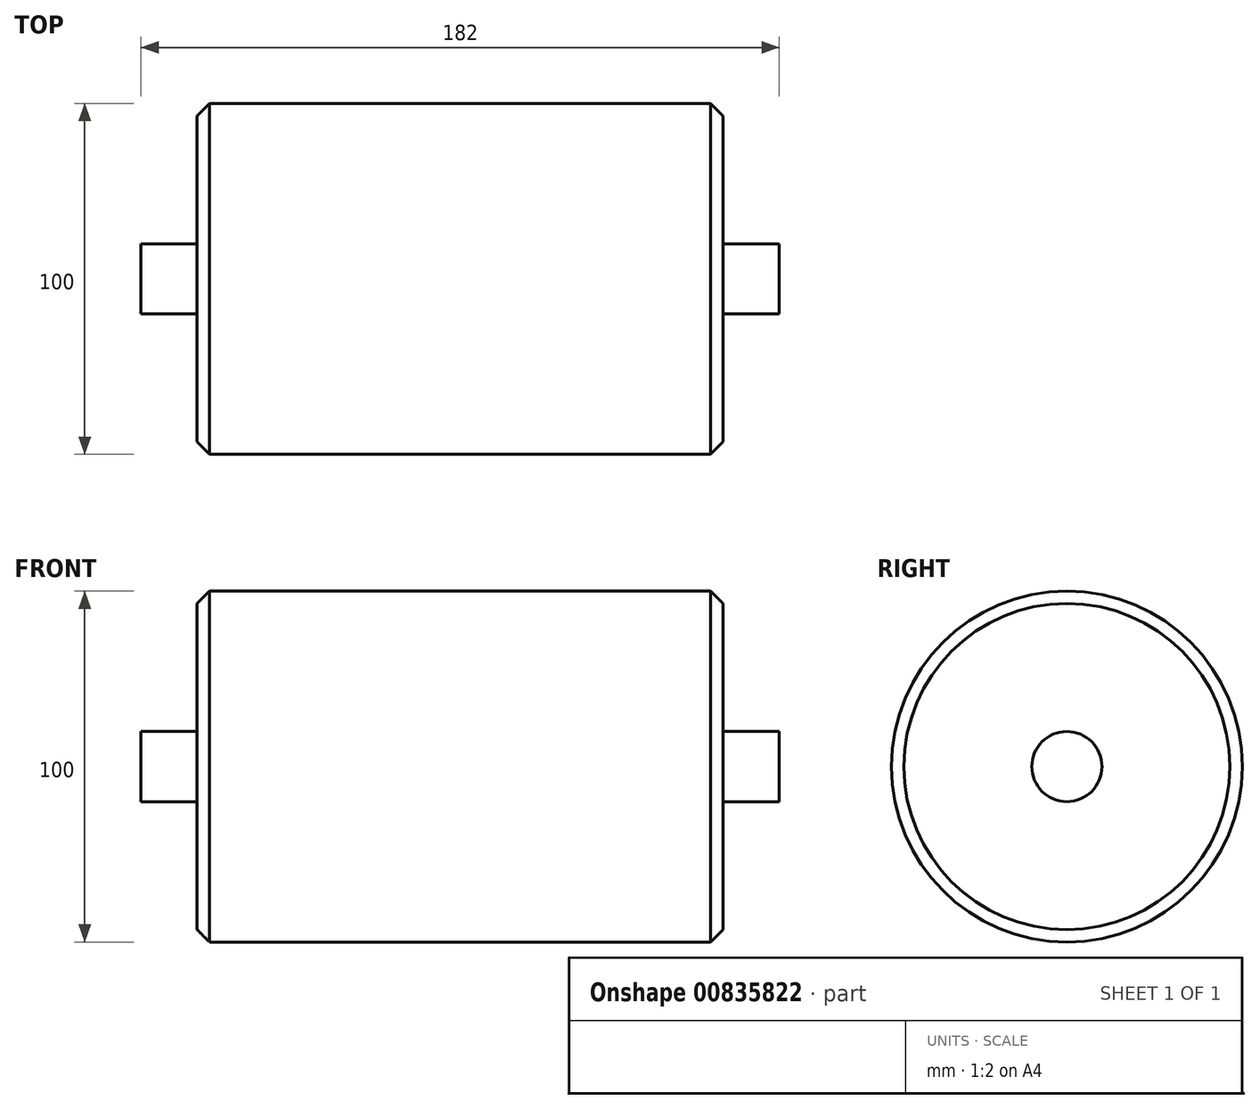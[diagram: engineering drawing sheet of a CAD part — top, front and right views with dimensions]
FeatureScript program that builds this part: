
annotation { "Feature Type Name" : "Feature", "Feature Type Description" : "" }
export const myFeature = defineFeature(function(context is Context, id is Id, definition is map)
    precondition{}
    {
        {
            var Q0;
            Q0=qCreatedBy(makeId("Top.planeOp"),FACE);
            var sketch = newSketch(context, id + "F0", { "sketchPlane" : qUnion([Q0])});
            skLineSegment(sketch, "E0", {"start": v(0, 0) * mm, "end": v(-91, 0) * mm});
            skLineSegment(sketch, "E1", {"start": v(-91, 0) * mm, "end": v(-91, 10) * mm});
            skLineSegment(sketch, "E2", {"start": v(-91, 10) * mm, "end": v(-75, 10) * mm});
            skLineSegment(sketch, "E3", {"start": v(-75, 10) * mm, "end": v(-75, 46.46) * mm});
            skLineSegment(sketch, "E4", {"start": v(-75, 46.46) * mm, "end": v(-71.46, 50) * mm});
            skLineSegment(sketch, "E5", {"start": v(-71.46, 50) * mm, "end": v(0, 50) * mm});
            skLineSegment(sketch, "E6.MirrorCS", {"start": v(71.46, 50) * mm, "end": v(0, 50) * mm});
            skLineSegment(sketch, "E7.MirrorCS", {"start": v(75, 10) * mm, "end": v(75, 46.46) * mm});
            skLineSegment(sketch, "E8.MirrorCS", {"start": v(91, 10) * mm, "end": v(75, 10) * mm});
            skLineSegment(sketch, "E9.MirrorCS", {"start": v(91, 0) * mm, "end": v(91, 10) * mm});
            skLineSegment(sketch, "E10.MirrorCS", {"start": v(0, 0) * mm, "end": v(91, 0) * mm});
            skLineSegment(sketch, "E11.MirrorCS", {"start": v(75, 46.46) * mm, "end": v(71.46, 50) * mm});
            skSolve(sketch);
        }
        {
            var Q0;
            Q0=makeQuery(id+"F0.imprint","IMPRINT",FACE,{"disambiguationData":[TD([[makeQuery(id+"F0.imprint","IMPRINT",EDGE,{"derivedFrom":sQuery(id+"F0.wireOp",EDGE,"E0")}),-1.0]])]});
            var Q1;
            Q1=sQuery(id+"F0.wireOp",EDGE,"E0");
            revolve(context, id + "F1", {"surfaceOperationType" : NewSurfaceOperationType.NEW, "entities" : qUnion([Q0]), "axis" : qUnion([Q1]), "revolveType" : RevolveType.FULL});
        }
    });
